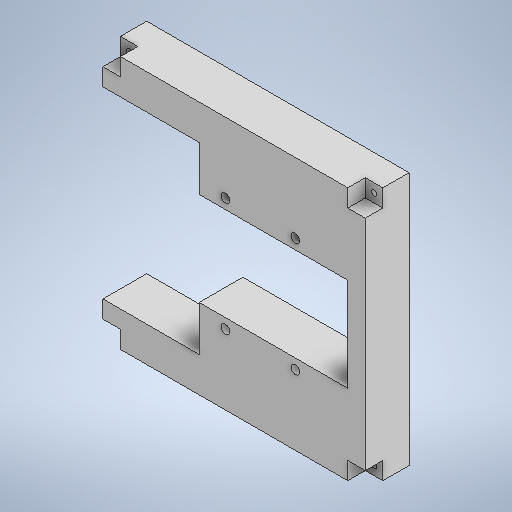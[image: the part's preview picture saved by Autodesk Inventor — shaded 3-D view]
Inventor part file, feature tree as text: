
AUTODESK INVENTOR PART (.ipt)
format: ipt  version: 2025.3 (Build 293356000, 356)  size: 635,392 bytes
history: native  units: mm
features: extrude x4, sketch x4, projected_geometry x3, other x1
ambient origin geometry x8: Origin, YZ Plane, XZ Plane, XY Plane, X Axis, Y Axis, Z Axis, Center Point
bodies: Body1 (feature_tree)
feature tree (12):
  other  "솔리드1"
  extrude  "돌출1"  Depth=290.0mm
  extrude  "돌출3"  Depth=300.0mm
  sketch  "스케치4"
  extrude  "돌출5"  Depth=25.0mm TaperAngle=0.0deg
  extrude  "돌출7"  Depth=105.0mm
  sketch  "스케치1"
  sketch  "스케치3"
  projected_geometry  "투영된 루프1"
  projected_geometry  "투영된 루프2"
  sketch  "스케치5"
  projected_geometry  "투영된 루프3"
